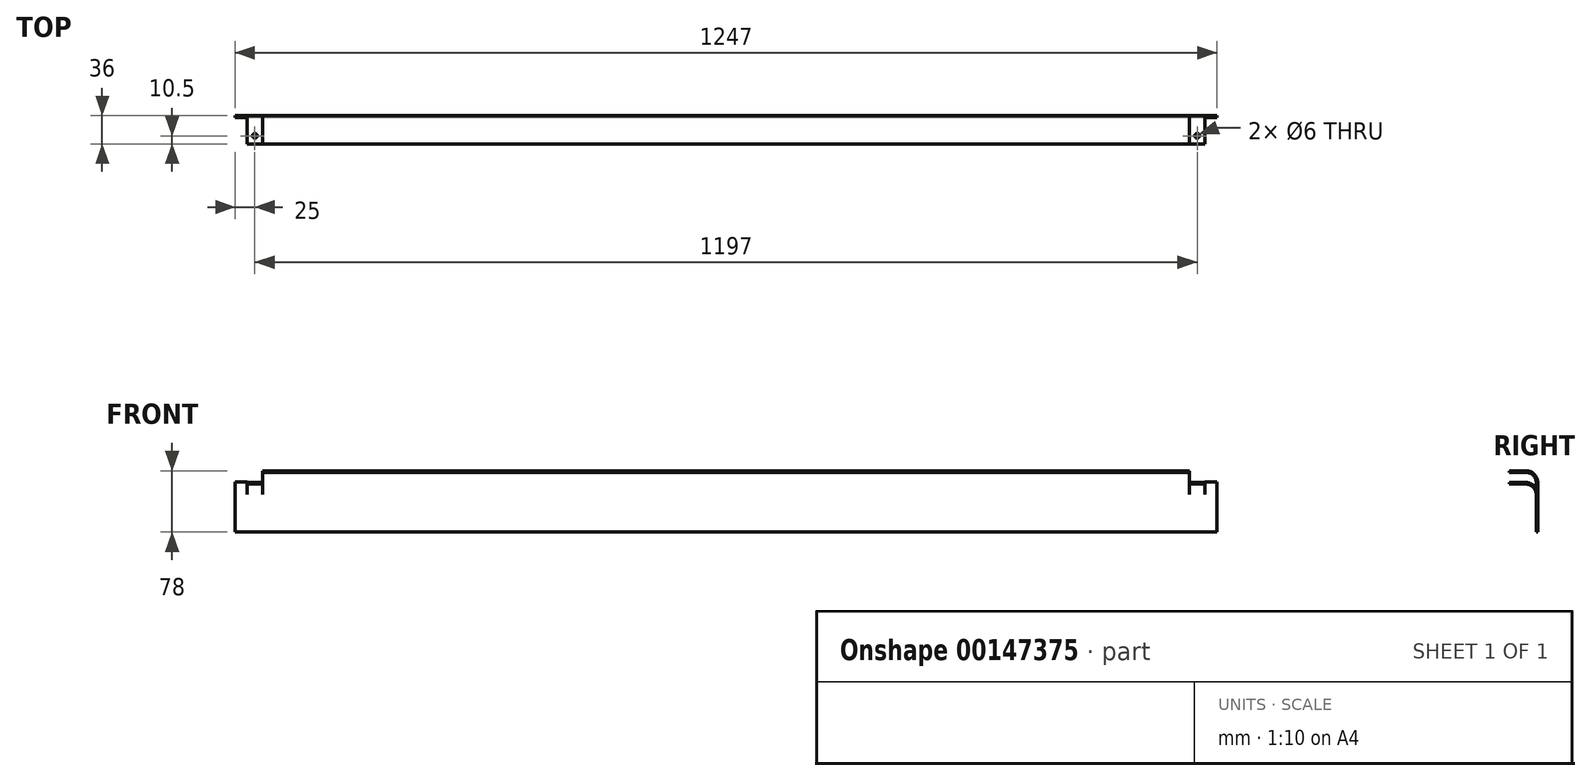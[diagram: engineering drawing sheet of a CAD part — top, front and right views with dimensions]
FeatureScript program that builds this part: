
annotation { "Feature Type Name" : "Feature", "Feature Type Description" : "" }
export const myFeature = defineFeature(function(context is Context, id is Id, definition is map)
    precondition{}
    {
        {
            var Q0;
            Q0=qCreatedBy(makeId("Right.planeOp"),FACE);
            var sketch = newSketch(context, id + "F0", { "sketchPlane" : qUnion([Q0])});
            skLineSegment(sketch, "E0.bottom", {"start": v(1, 32) * mm, "end": v(-1, 32) * mm});
            skLineSegment(sketch, "E0.top", {"start": v(1, -32) * mm, "end": v(-1, -32) * mm});
            skLineSegment(sketch, "E0.left", {"start": v(1, 32) * mm, "end": v(1, -32) * mm});
            skLineSegment(sketch, "E0.right", {"start": v(-1, 32) * mm, "end": v(-1, -32) * mm});
            skPoint(sketch, "E0.middle", {"position": v(0, 0) * mm});
            skSolve(sketch);
        }
        {
            var Q0;
            Q0=makeQuery(id+"F0.imprint","IMPRINT",FACE,{"disambiguationData":[TD([[makeQuery(id+"F0.imprint","IMPRINT",EDGE,{"derivedFrom":sQuery(id+"F0.wireOp",EDGE,"E0.bottom")}),1.0]])]});
            extrude(context, id + "F1", {"entities" : qUnion([Q0]), "depth" : 15 * mm});
        }
        {
            var Q0;
            Q0=makeQuery(id+"F1.opExtrude","CAP_FACE",FACE,{"disambiguationData":[OSD([sQuery(id+"F0.wireOp",EDGE,"E0.bottom"),sQuery(id+"F0.wireOp",EDGE,"E0.top"),sQuery(id+"F0.wireOp",EDGE,"E0.left"),sQuery(id+"F0.wireOp",EDGE,"E0.right")])],"isStart":false});
            var sketch = newSketch(context, id + "F2", { "sketchPlane" : qUnion([Q0])});
            skLineSegment(sketch, "E1.bottom", {"start": v(1, -32) * mm, "end": v(-1, -32) * mm});
            skLineSegment(sketch, "E1.top", {"start": v(-14, 31) * mm, "end": v(-35, 31) * mm});
            skLineSegment(sketch, "E1.left", {"start": v(1, -32) * mm, "end": v(1, 16) * mm});
            skLineSegment(sketch, "E1.right", {"start": v(-35, 29) * mm, "end": v(-35, 31) * mm});
            skLineSegment(sketch, "E2.top", {"start": v(-35, 29) * mm, "end": v(-14, 29) * mm});
            skLineSegment(sketch, "E2.right", {"start": v(-1, -32) * mm, "end": v(-1, 16) * mm});
            skPoint(sketch, "E3.visualSharp", {"position": v(-1, 29) * mm});
            skArc(sketch, "E3.filletArc", {"start": v(-1, 16) * mm, "mid": v(-4.8, 25.2) * mm, "end": v(-14, 29) * mm});
            skPoint(sketch, "E4.visualSharp", {"position": v(1, 31) * mm});
            skArc(sketch, "E4.filletArc", {"start": v(1, 16) * mm, "mid": v(-3.4, 26.6) * mm, "end": v(-14, 31) * mm});
            skSolve(sketch);
        }
        {
            var Q0;
            Q0 = qSketchRegion(id + "F2", true);
            extrude(context, id + "F3", {"entities" : qUnion([Q0]), "operationType" : NewBodyOperationType.ADD, "depth" : 20 * mm});
        }
        {
            var Q0;
            Q0=makeQuery(id+"F3.opExtrude","CAP_FACE",FACE,{"disambiguationData":[OSD([sQuery(id+"F2.wireOp",EDGE,"E1.bottom"),sQuery(id+"F2.wireOp",EDGE,"E1.top"),sQuery(id+"F2.wireOp",EDGE,"E1.left"),sQuery(id+"F2.wireOp",EDGE,"E1.right"),sQuery(id+"F2.wireOp",EDGE,"E2.top"),sQuery(id+"F2.wireOp",EDGE,"E2.right"),sQuery(id+"F2.wireOp",EDGE,"E3.filletArc"),sQuery(id+"F2.wireOp",EDGE,"E4.filletArc")])],"isStart":false});
            var sketch = newSketch(context, id + "F4", { "sketchPlane" : qUnion([Q0])});
            skLineSegment(sketch, "E5.bottom", {"start": v(1, -32) * mm, "end": v(-1, -32) * mm});
            skLineSegment(sketch, "E5.top", {"start": v(-14, 46) * mm, "end": v(-35, 46) * mm});
            skLineSegment(sketch, "E5.left", {"start": v(1, -32) * mm, "end": v(1, 31) * mm});
            skLineSegment(sketch, "E5.right", {"start": v(-35, 44) * mm, "end": v(-35, 46) * mm});
            skLineSegment(sketch, "E6.top", {"start": v(-35, 44) * mm, "end": v(-14, 44) * mm});
            skLineSegment(sketch, "E6.right", {"start": v(-1, -32) * mm, "end": v(-1, 31) * mm});
            skPoint(sketch, "E7.visualSharp", {"position": v(-1, 44) * mm});
            skArc(sketch, "E7.filletArc", {"start": v(-1, 31) * mm, "mid": v(-4.8, 40.2) * mm, "end": v(-14, 44) * mm});
            skPoint(sketch, "E8.visualSharp", {"position": v(1, 46) * mm});
            skArc(sketch, "E8.filletArc", {"start": v(1, 31) * mm, "mid": v(-3.4, 41.6) * mm, "end": v(-14, 46) * mm});
            skSolve(sketch);
        }
        {
            var Q0;
            Q0 = qSketchRegion(id + "F4", true);
            extrude(context, id + "F5", {"entities" : qUnion([Q0]), "operationType" : NewBodyOperationType.ADD, "depth" : 1177 * mm});
        }
        {
            var Q0;
            Q0=makeQuery(id+"F5.opExtrude","CAP_FACE",FACE,{"disambiguationData":[OSD([sQuery(id+"F4.wireOp",EDGE,"E5.bottom"),sQuery(id+"F4.wireOp",EDGE,"E5.top"),sQuery(id+"F4.wireOp",EDGE,"E5.left"),sQuery(id+"F4.wireOp",EDGE,"E5.right"),sQuery(id+"F4.wireOp",EDGE,"E6.top"),sQuery(id+"F4.wireOp",EDGE,"E6.right"),sQuery(id+"F4.wireOp",EDGE,"E7.filletArc"),sQuery(id+"F4.wireOp",EDGE,"E8.filletArc")])],"isStart":false});
            var sketch = newSketch(context, id + "F6", { "sketchPlane" : qUnion([Q0])});
            skLineSegment(sketch, "E9.bottom", {"start": v(1, -32) * mm, "end": v(-1, -32) * mm});
            skLineSegment(sketch, "E9.top", {"start": v(-14, 31) * mm, "end": v(-35, 31) * mm});
            skLineSegment(sketch, "E9.left", {"start": v(1, -32) * mm, "end": v(1, 16) * mm});
            skLineSegment(sketch, "E9.right", {"start": v(-35, 29) * mm, "end": v(-35, 31) * mm});
            skLineSegment(sketch, "E10.top", {"start": v(-35, 29) * mm, "end": v(-14, 29) * mm});
            skLineSegment(sketch, "E10.right", {"start": v(-1, -32) * mm, "end": v(-1, 16) * mm});
            skPoint(sketch, "E11.visualSharp", {"position": v(-1, 29) * mm});
            skArc(sketch, "E11.filletArc", {"start": v(-1, 16) * mm, "mid": v(-4.8, 25.2) * mm, "end": v(-14, 29) * mm});
            skPoint(sketch, "E12.visualSharp", {"position": v(1, 31) * mm});
            skArc(sketch, "E12.filletArc", {"start": v(1, 16) * mm, "mid": v(-3.4, 26.6) * mm, "end": v(-14, 31) * mm});
            skSolve(sketch);
        }
        {
            var Q0;
            Q0 = qSketchRegion(id + "F6", true);
            extrude(context, id + "F7", {"entities" : qUnion([Q0]), "operationType" : NewBodyOperationType.ADD, "depth" : 20 * mm});
        }
        {
            var Q0;
            Q0=makeQuery(id+"F7.opExtrude","CAP_FACE",FACE,{"disambiguationData":[OSD([sQuery(id+"F6.wireOp",EDGE,"E9.bottom"),sQuery(id+"F6.wireOp",EDGE,"E9.top"),sQuery(id+"F6.wireOp",EDGE,"E9.left"),sQuery(id+"F6.wireOp",EDGE,"E9.right"),sQuery(id+"F6.wireOp",EDGE,"E10.top"),sQuery(id+"F6.wireOp",EDGE,"E10.right"),sQuery(id+"F6.wireOp",EDGE,"E11.filletArc"),sQuery(id+"F6.wireOp",EDGE,"E12.filletArc")])],"isStart":false});
            var sketch = newSketch(context, id + "F8", { "sketchPlane" : qUnion([Q0])});
            skLineSegment(sketch, "E13.bottom", {"start": v(1, -32) * mm, "end": v(-1, -32) * mm});
            skLineSegment(sketch, "E13.top", {"start": v(1, 32) * mm, "end": v(-1, 32) * mm});
            skLineSegment(sketch, "E13.left", {"start": v(1, -32) * mm, "end": v(1, 32) * mm});
            skLineSegment(sketch, "E13.right", {"start": v(-1, -32) * mm, "end": v(-1, 32) * mm});
            skSolve(sketch);
        }
        {
            var Q0;
            Q0 = qSketchRegion(id + "F8", true);
            extrude(context, id + "F9", {"entities" : qUnion([Q0]), "operationType" : NewBodyOperationType.ADD, "depth" : 15 * mm});
        }
        {
            var Q0;
            Q0=makeQuery(id+"F7.opExtrude","SWEPT_FACE",FACE,{"disambiguationData":[OSD([sQuery(id+"F6.wireOp",EDGE,"E9.top")])]});
            var sketch = newSketch(context, id + "F10", { "sketchPlane" : qUnion([Q0])});
            skCircle(sketch, "E14", {"center": v(1222, -24.5) * mm, "radius": 3 * mm});
            skPoint(sketch, "E15.orphan", {"position": v(1222, -35) * mm});
            skSolve(sketch);
        }
        {
            var Q0;
            Q0 = qSketchRegion(id + "F10", true);
            extrude(context, id + "F11", {"entities" : qUnion([Q0]), "operationType" : NewBodyOperationType.REMOVE, "oppositeDirection" : true, "depth" : 2 * mm});
        }
        {
            var Q0;
            Q0=makeQuery(id+"F3.opExtrude","SWEPT_FACE",FACE,{"disambiguationData":[OSD([sQuery(id+"F2.wireOp",EDGE,"E1.top")])]});
            var sketch = newSketch(context, id + "F12", { "sketchPlane" : qUnion([Q0])});
            skCircle(sketch, "E16", {"center": v(25, -24.5) * mm, "radius": 3 * mm});
            skPoint(sketch, "E17.start.orphan", {"position": v(25, -35) * mm});
            skSolve(sketch);
        }
        {
            var Q0;
            Q0 = qSketchRegion(id + "F12", true);
            extrude(context, id + "F13", {"entities" : qUnion([Q0]), "operationType" : NewBodyOperationType.REMOVE, "oppositeDirection" : true, "depth" : 2 * mm});
        }
    });
